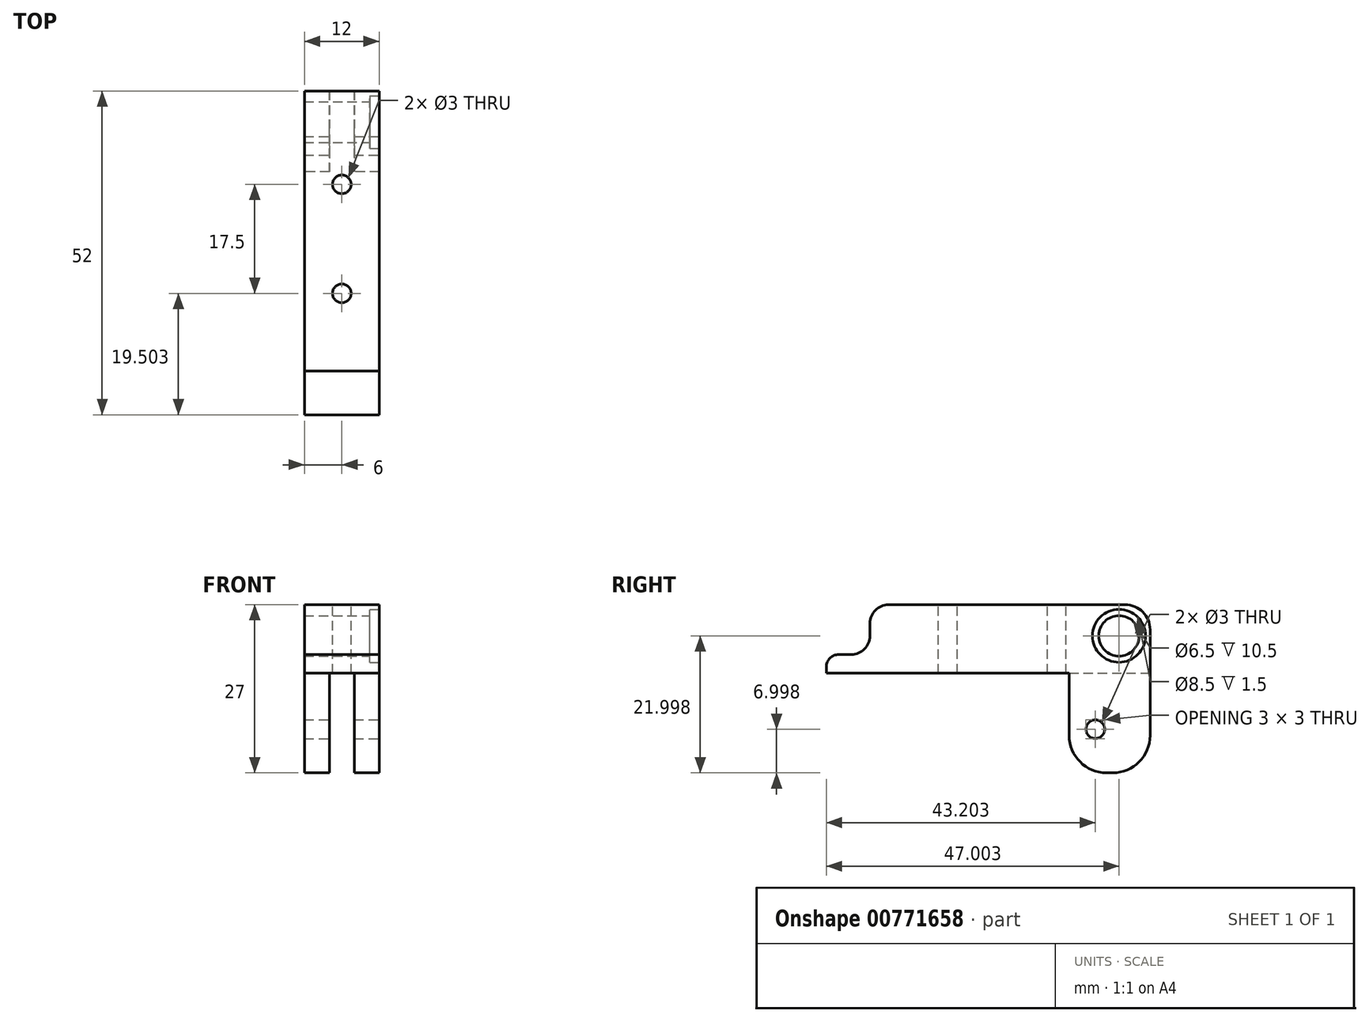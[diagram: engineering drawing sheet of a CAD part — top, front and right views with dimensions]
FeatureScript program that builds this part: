
annotation { "Feature Type Name" : "Feature", "Feature Type Description" : "" }
export const myFeature = defineFeature(function(context is Context, id is Id, definition is map)
    precondition{}
    {
        {
            var Q0;
            Q0=qCreatedBy(makeId("Right.planeOp"),FACE);
            var sketch = newSketch(context, id + "F0", { "sketchPlane" : qUnion([Q0])});
            skLineSegment(sketch, "E0", {"start": v(-22.15, 20.84) * mm, "end": v(22.85, 20.84) * mm});
            skLineSegment(sketch, "E1", {"start": v(22.85, 20.84) * mm, "end": v(22.85, -6.16) * mm});
            skLineSegment(sketch, "E2", {"start": v(22.85, -6.16) * mm, "end": v(9.85, -6.16) * mm});
            skLineSegment(sketch, "E3", {"start": v(9.85, -6.16) * mm, "end": v(9.85, 9.84) * mm});
            skLineSegment(sketch, "E4", {"start": v(9.85, 9.84) * mm, "end": v(-29.15, 9.84) * mm});
            skLineSegment(sketch, "E5", {"start": v(-29.15, 9.84) * mm, "end": v(-29.15, 12.84) * mm});
            skLineSegment(sketch, "E6", {"start": v(-29.15, 12.84) * mm, "end": v(-22.15, 12.84) * mm});
            skLineSegment(sketch, "E7", {"start": v(-22.15, 12.84) * mm, "end": v(-22.15, 20.84) * mm});
            skSolve(sketch);
        }
        {
            var Q0;
            Q0 = qSketchRegion(id + "F0", true);
            extrude(context, id + "F1", {"entities" : qUnion([Q0]), "depth" : 12 * mm, "offsetDistance" : 25 * mm});
        }
        {
            var Q0;
            Q0=makeQuery(id+"F1.opExtrude","CAP_FACE",FACE,{"disambiguationData":[OSD([sQuery(id+"F0.wireOp",EDGE,"E0"),sQuery(id+"F0.wireOp",EDGE,"E1"),sQuery(id+"F0.wireOp",EDGE,"E2"),sQuery(id+"F0.wireOp",EDGE,"E3"),sQuery(id+"F0.wireOp",EDGE,"E4"),sQuery(id+"F0.wireOp",EDGE,"E5"),sQuery(id+"F0.wireOp",EDGE,"E6"),sQuery(id+"F0.wireOp",EDGE,"E7")])],"isStart":false});
            var sketch = newSketch(context, id + "F2", { "sketchPlane" : qUnion([Q0])});
            skCircle(sketch, "E8", {"center": v(17.85, 15.84) * mm, "radius": 3.25 * mm});
            skSolve(sketch);
        }
        {
            var Q0;
            Q0 = qSketchRegion(id + "F2", true);
            extrude(context, id + "F3", {"entities" : qUnion([Q0]), "operationType" : NewBodyOperationType.REMOVE, "endBound" : BoundingType.THROUGH_ALL, "oppositeDirection" : true, "depth" : 25 * mm, "offsetDistance" : 25 * mm});
        }
        {
            var Q0;
            {var subQ0=sQuery(id+"F0.wireOp",EDGE,"E0");Q0=makeQuery(id+"FR67hCXwh2B9Ixh_1.boolean.opBoolean","MERGE",FACE,{"derivedFrom":[makeQuery(id+"F1.opExtrude","SWEPT_FACE",FACE,{"disambiguationData":[OSD([subQ0])]}),makeQuery(id+"FR67hCXwh2B9Ixh_1.opExtrude","SWEPT_FACE",FACE,{"disambiguationData":[OSD([subQ0])]})]});}
            var sketch = newSketch(context, id + "F4", { "sketchPlane" : qUnion([Q0])});
            skCircle(sketch, "E9", {"center": v(6, 7.85) * mm, "radius": 1.5 * mm});
            skCircle(sketch, "E10", {"center": v(6, -9.65) * mm, "radius": 1.5 * mm});
            skSolve(sketch);
        }
        {
            var Q0;
            Q0=makeQuery(id+"F1.opExtrude","CAP_FACE",FACE,{"disambiguationData":[OSD([sQuery(id+"F0.wireOp",EDGE,"E0"),sQuery(id+"F0.wireOp",EDGE,"E1"),sQuery(id+"F0.wireOp",EDGE,"E2"),sQuery(id+"F0.wireOp",EDGE,"E3"),sQuery(id+"F0.wireOp",EDGE,"E4"),sQuery(id+"F0.wireOp",EDGE,"E5"),sQuery(id+"F0.wireOp",EDGE,"E6"),sQuery(id+"F0.wireOp",EDGE,"E7")])],"isStart":false});
            var sketch = newSketch(context, id + "F5", { "sketchPlane" : qUnion([Q0])});
            skCircle(sketch, "E11", {"center": v(17.85, 15.84) * mm, "radius": 4.25 * mm});
            skSolve(sketch);
        }
        {
            var Q0;
            Q0 = qSketchRegion(id + "F5", true);
            extrude(context, id + "F6", {"entities" : qUnion([Q0]), "operationType" : NewBodyOperationType.REMOVE, "oppositeDirection" : true, "depth" : 1.5 * mm, "offsetDistance" : 25 * mm});
        }
        {
            var Q0;
            Q0 = qSketchRegion(id + "F4", true);
            extrude(context, id + "F7", {"entities" : qUnion([Q0]), "operationType" : NewBodyOperationType.REMOVE, "endBound" : BoundingType.THROUGH_ALL, "oppositeDirection" : true, "depth" : 25 * mm, "offsetDistance" : 25 * mm});
        }
        {
            var Q0;
            Q0=makeQuery(id+"F1.opExtrude","SWEPT_EDGE",EDGE,{"disambiguationData":[OSD([sQuery(id+"F0.wireOp",EDGE,"E0"),sQuery(id+"F0.wireOp",EDGE,"E1")])]});
            fillet(context, id + "F8", {"entities" : qUnion([Q0]), "radius" : 4 * mm, "tangentPropagation" : true, "allowEdgeOverflow" : false});
        }
        {
            var Q0;
            Q0=makeQuery(id+"F1.opExtrude","SWEPT_EDGE",EDGE,{"disambiguationData":[OSD([sQuery(id+"F0.wireOp",EDGE,"E0"),sQuery(id+"F0.wireOp",EDGE,"E7")])]});
            var Q1;
            Q1=makeQuery(id+"F1.opExtrude","SWEPT_EDGE",EDGE,{"disambiguationData":[OSD([sQuery(id+"F0.wireOp",EDGE,"E6"),sQuery(id+"F0.wireOp",EDGE,"E7")])]});
            fillet(context, id + "F9", {"entities" : qUnion([Q0, Q1]), "radius" : 3 * mm, "tangentPropagation" : true, "allowEdgeOverflow" : false});
        }
        {
            var Q0;
            Q0=makeQuery(id+"F1.opExtrude","SWEPT_EDGE",EDGE,{"disambiguationData":[OSD([sQuery(id+"F0.wireOp",EDGE,"E5"),sQuery(id+"F0.wireOp",EDGE,"E6")])]});
            fillet(context, id + "F10", {"entities" : qUnion([Q0]), "radius" : 2 * mm, "tangentPropagation" : true, "allowEdgeOverflow" : false});
        }
        {
            var Q0;
            Q0=makeQuery(id+"F1.opExtrude","CAP_FACE",FACE,{"disambiguationData":[OSD([sQuery(id+"F0.wireOp",EDGE,"E0"),sQuery(id+"F0.wireOp",EDGE,"E1"),sQuery(id+"F0.wireOp",EDGE,"E2"),sQuery(id+"F0.wireOp",EDGE,"E3"),sQuery(id+"F0.wireOp",EDGE,"E4"),sQuery(id+"F0.wireOp",EDGE,"E5"),sQuery(id+"F0.wireOp",EDGE,"E6"),sQuery(id+"F0.wireOp",EDGE,"E7")])],"isStart":false});
            var sketch = newSketch(context, id + "F11", { "sketchPlane" : qUnion([Q0])});
            skCircle(sketch, "E12", {"center": v(14.05, 0.84) * mm, "radius": 1.5 * mm});
            skSolve(sketch);
        }
        {
            var Q0;
            Q0 = qSketchRegion(id + "F11", true);
            extrude(context, id + "F12", {"entities" : qUnion([Q0]), "operationType" : NewBodyOperationType.REMOVE, "endBound" : BoundingType.THROUGH_ALL, "oppositeDirection" : true, "depth" : 25 * mm, "offsetDistance" : 25 * mm});
        }
        {
            var Q0;
            Q0=makeQuery(id+"F1.opExtrude","SWEPT_FACE",FACE,{"disambiguationData":[OSD([sQuery(id+"F0.wireOp",EDGE,"E2")])]});
            var sketch = newSketch(context, id + "F13", { "sketchPlane" : qUnion([Q0])});
            skLineSegment(sketch, "E13.bottom", {"start": v(4, -9.85) * mm, "end": v(8, -9.85) * mm});
            skLineSegment(sketch, "E13.top", {"start": v(4, -22.85) * mm, "end": v(8, -22.85) * mm});
            skLineSegment(sketch, "E13.left", {"start": v(4, -9.85) * mm, "end": v(4, -22.85) * mm});
            skLineSegment(sketch, "E13.right", {"start": v(8, -9.85) * mm, "end": v(8, -22.85) * mm});
            skSolve(sketch);
        }
        {
            var Q0;
            Q0 = qSketchRegion(id + "F13", true);
            extrude(context, id + "F14", {"entities" : qUnion([Q0]), "operationType" : NewBodyOperationType.REMOVE, "oppositeDirection" : true, "depth" : 16 * mm, "offsetDistance" : 25 * mm});
        }
        {
            var Q0;
            {var subQ0=sQuery(id+"F0.wireOp",EDGE,"E3");var subQ1=sQuery(id+"F0.wireOp",EDGE,"E2");Q0=makeQuery(id+"F14.boolean.opBoolean","SPLIT",EDGE,{"disambiguationData":[TD([makeQuery(id+"F14.opExtrude","SWEPT_FACE",FACE,{"disambiguationData":[OSD([sQuery(id+"F13.wireOp",EDGE,"E13.right")])]})])],"derivedFrom":makeQuery(id+"F1.opExtrude","SWEPT_EDGE",EDGE,{"disambiguationData":[OSD([subQ1,subQ0])]})});}
            var Q1;
            {var subQ0=sQuery(id+"F0.wireOp",EDGE,"E2");var subQ1=sQuery(id+"F0.wireOp",EDGE,"E1");Q1=makeQuery(id+"F14.boolean.opBoolean","SPLIT",EDGE,{"disambiguationData":[TD([makeQuery(id+"F14.opExtrude","SWEPT_FACE",FACE,{"disambiguationData":[OSD([sQuery(id+"F13.wireOp",EDGE,"E13.right")])]})])],"derivedFrom":makeQuery(id+"F1.opExtrude","SWEPT_EDGE",EDGE,{"disambiguationData":[OSD([subQ1,subQ0])]})});}
            var Q2;
            {var subQ0=sQuery(id+"F0.wireOp",EDGE,"E2");var subQ1=sQuery(id+"F0.wireOp",EDGE,"E1");Q2=makeQuery(id+"F14.boolean.opBoolean","SPLIT",EDGE,{"disambiguationData":[TD([makeQuery(id+"F14.opExtrude","SWEPT_FACE",FACE,{"disambiguationData":[OSD([sQuery(id+"F13.wireOp",EDGE,"E13.left")])]})])],"derivedFrom":makeQuery(id+"F1.opExtrude","SWEPT_EDGE",EDGE,{"disambiguationData":[OSD([subQ1,subQ0])]})});}
            var Q3;
            {var subQ0=sQuery(id+"F0.wireOp",EDGE,"E3");var subQ1=sQuery(id+"F0.wireOp",EDGE,"E2");Q3=makeQuery(id+"F14.boolean.opBoolean","SPLIT",EDGE,{"disambiguationData":[TD([makeQuery(id+"F14.opExtrude","SWEPT_FACE",FACE,{"disambiguationData":[OSD([sQuery(id+"F13.wireOp",EDGE,"E13.left")])]})])],"derivedFrom":makeQuery(id+"F1.opExtrude","SWEPT_EDGE",EDGE,{"disambiguationData":[OSD([subQ1,subQ0])]})});}
            fillet(context, id + "F15", {"entities" : qUnion([Q0, Q1, Q2, Q3]), "radius" : 6 * mm, "tangentPropagation" : true, "allowEdgeOverflow" : false});
        }
    });
